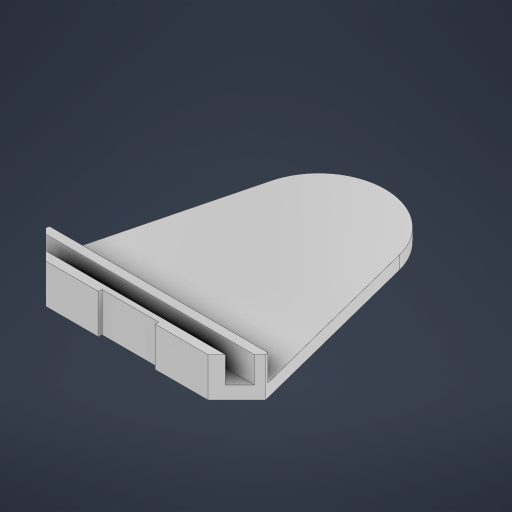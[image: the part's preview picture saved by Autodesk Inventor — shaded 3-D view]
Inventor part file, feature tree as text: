
AUTODESK INVENTOR PART (.ipt)
format: ipt  version: 2024 (Build 280153000, 153)  size: 235,008 bytes
history: native  units: mm
features: extrude x3, sketch x3, chamfer x1, projected_geometry x1
ambient origin geometry x8: Origin, YZ Plane, XZ Plane, XY Plane, X Axis, Y Axis, Z Axis, Center Point
bodies: Solid1 (feature_tree)
feature tree (8):
  extrude  "Extrusion1"  Depth=15.0mm TaperAngle=45.0deg
  chamfer  "Chamfer1"  Distance=16.5mm
  extrude  "Extrusion2"  Depth=30.0mm TaperAngle=0.0deg
  extrude  "Extrusion3"  Depth=65.0mm
  sketch  "Sketch1"  dims[d0=15.0mm d1=0.0mm d2=33.0mm d3=2.0mm d4=45.0deg]
  sketch  "Sketch4"  dims[d5=10.0mm]
  projected_geometry  "Projected Loop2"
  sketch  "Sketch5"  dims[d6=10.0mm d7=16.5mm d8=30.0mm d9=0.0mm d10=65.0mm d11=60.5mm d12=60.5mm d13=4.0mm d14=0.0mm]
